# Revit family: O3.25UM_NRG -All - Linked Data
name_source: partatom
category: Mechanical Equipment
units: mm (PartAtom-declared; Revit-internal decimal feet)

## family parameters
Always vertical = Yes
Cut with Voids When Loaded = No
OmniClass Number = 23.40.40.11.17
OmniClass Title = Refrigerated Cases
Part Type = Normal
Room Calculation Point = No
Round Connector Dimension = Use Radius
Shared = No
Work Plane-Based = Yes

## types (9) — shared parameters
12" Shelf = Yes
14" Shelf = Yes
16" Shelf = Yes
BOTTOM ELECTRICAL = Yes
BOTTOM REFRIGERATION PIPING = Yes
Certifications = NSF 7, UL471, CSA
DATE = 03/29/2016
DESIGNERS NAME = SHIDDRAMESH
DRAIN PIPING = Yes
Default Elevation = 48"
Description = Multi-Deck Merchandiser with Synerg-E™
EQUIPMENT DESCRIPTION = Multi-Deck Merchandiser with Synerg-E™
EQUIPMENT MARK = O3.25UM-NRG
Ends = Yes
GLASS = Glass
Height = 57 7/8"
How Many Defrosts Per Day = 6
Island Discharge Air Velocity (FPM) = 150 FPM
Island Superheat @ Bulb Set Point (°F) = 6-8 °F
Island Timed-Off Fail-Safe (Min) = 30 (Min)
Island Timed-Off Termination Temp (°F) = 42 °F
Item Description = Multi-Deck Merchandiser with Synerg-E™
LF STD END = Yes
Legend Number = O3.25UM-NRG
Manufacturer = HILL PHOENIX
Model = O3.25UM-NRG
Number of Shelf = 3
PAINTED METAL UPPER SHELF = PAINTED SHELVES
REAR REFRIGERATION PIPING = Yes
REFRIGERATION PIPING = COPPER PIPE
RT STD END = Yes
STAINLESS STEEL = GALVANIZED STEEL
Standard Power Amps = 0 A
TOP ELECTRICAL = Yes
TOP REFRIGERATION PIPING = Yes
URL = http://www.hillphoenix.com
Width = 43 1/4"

## per-type parameters (varying)
| type | DRAIN LINE | High Efficiency Amps | High Efficiency Watts | High Power (Cornice) Amps | High Power (Cornice) Watts | Island Application | Island BTUH Conventional | Island BTUH Parallel | Island Discharge Air(°F) | Island Evaporator (°F) | Island Front Sill Height | Length | Light Length | Lights Per Row | Number of Fans | Refgn | Shelf distance | Standard Power Watts |
| 04' | 36" | 0 A | 0 W | 0 A | 0 W | Dairy / Deli / Produce | 960 | 840 | 31 °F | 28 °F | All | 48" | 0" | 0 | 0 | 22 3/4" | 36" | 0 W |
| 06' | 36" | 0 A | 0 W | 0 A | 0 W | Dairy / Deli / Produce | 960 | 840 | 31 °F | 28 °F | All | 72" | 0" | 0 | 0 | 28 5/8" | 36" | 0 W |
| 08' | 48" | 0 A | 0 W | 0 A | 0 W | Dairy / Deli / Produce | 960 | 840 | 31 °F | 28 °F | All | 96" | 0" | 0 | 0 | 28 5/8" | 48" | 0 W |
| 12' | 72" | 0 A | 0 W | 0 A | 0 W | Dairy / Deli / Produce | 960 | 840 | 31 °F | 28 °F | All | 144" | 0" | 0 | 0 | 28 5/8" | 48" | 0 W |
| 04' Dairy / Deli / Produce | 36" | 0 A | 14 W | 0 A | 22 W | Dairy / Deli / Produce | 960 | 840 | 31 °F | 28 °F | All | 48" | 48" | 1 | 1 | 12 3/8" | 36" | 12 W |
| 06' Dairy / Deli / Produce | 36" | 0 A | 28 W | 0 A | 30 W | Dairy / Deli / Produce | 960 | 840 | 31 °F | 28 °F | All | 72" | 36" | 2 | 2 | 12 3/8" | 36" | 17 W |
| 08' Dairy / Deli / Produce | 48" | 0 A | 28 W | 36 A | 43 W | Dairy / Deli / Produce | 960 | 840 | 31 °F | 28 °F | All | 96" | 48" | 2 | 2 | 12 3/8" | 48" | 24 W |
| 12' Dairy / Deli / Produce | 72" | 1 A | 42 W | 1 A | 65 W | Dairy / Deli / Produce | 960 | 840 | 31 °F | 28 °F | All | 144" | 48" | 3 | 3 | 12 3/8" | 48" | 36 W |
| 06' Meat | 36" | 0 A | 28 W | 0 A | 30 W | Meat | 949 | 830 | 30 °F | 26 °F | Extended | 72" | 36" | 2 | 2 | 28 5/8" | 36" | 17 W |

## geometry (parser evidence)
native form markers: Blend x8, Sweep x2
no freeform markers — native parametric forms only
